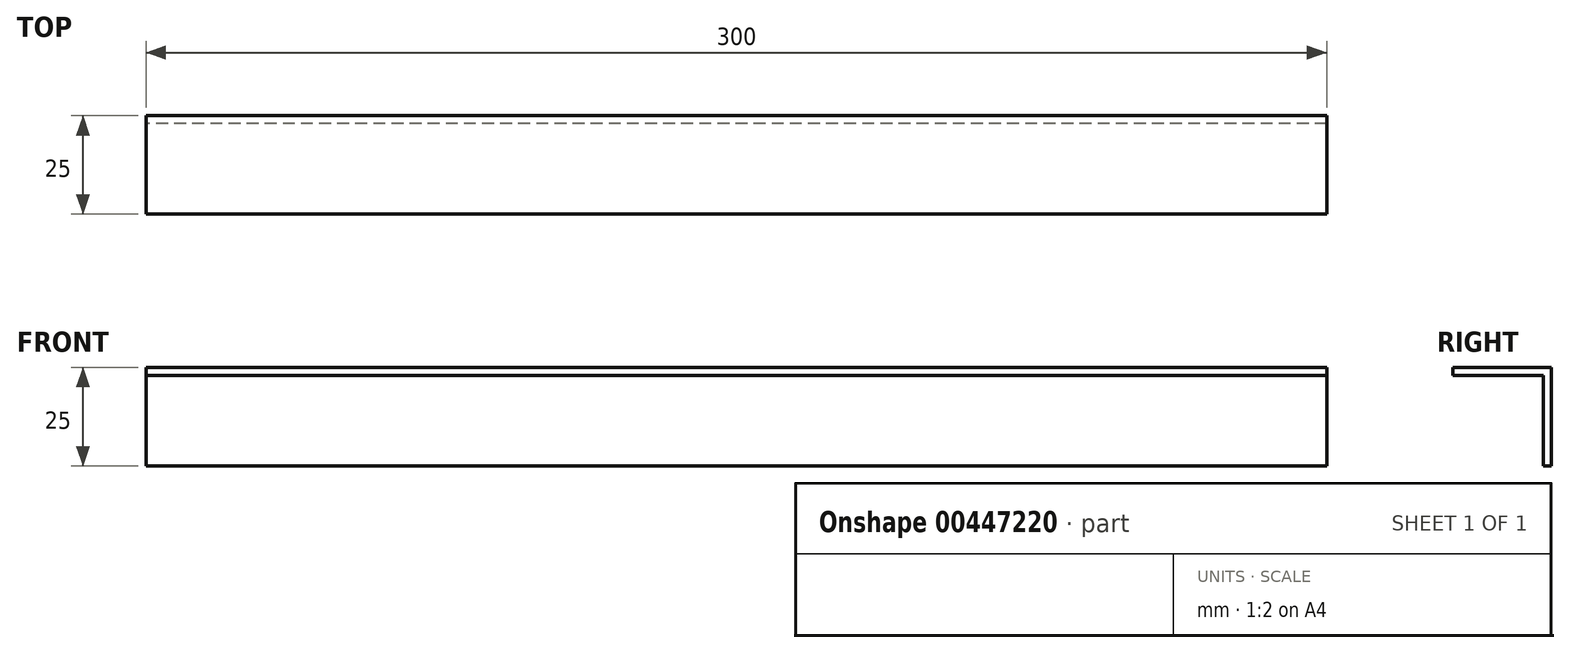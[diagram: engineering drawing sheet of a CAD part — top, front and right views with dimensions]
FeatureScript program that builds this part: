
annotation { "Feature Type Name" : "Feature", "Feature Type Description" : "" }
export const myFeature = defineFeature(function(context is Context, id is Id, definition is map)
    precondition{}
    {
        {
            var Q0;
            Q0=qCreatedBy(makeId("Top.planeOp"),FACE);
            var sketch = newSketch(context, id + "F0", { "sketchPlane" : qUnion([Q0])});
            skCircle(sketch, "E0", {"center": v(0, 0) * mm, "radius": 300 * mm, "construction": true});
            skPoint(sketch, "E1", {"position": v(150, -259.8) * mm});
            skSolve(sketch);
        }
        {
            var Q0;
            Q0=qCreatedBy(makeId("Right.planeOp"),FACE);
            var sketch = newSketch(context, id + "F1", { "sketchPlane" : qUnion([Q0])});
            skLineSegment(sketch, "E2", {"start": v(-259.8, 0) * mm, "end": v(-234.8, 0) * mm});
            skLineSegment(sketch, "E3", {"start": v(-234.8, 0) * mm, "end": v(-234.8, -25) * mm});
            skLineSegment(sketch, "E4", {"start": v(-234.8, -25) * mm, "end": v(-236.8, -25) * mm});
            skLineSegment(sketch, "E5", {"start": v(-236.8, -25) * mm, "end": v(-236.8, -2) * mm});
            skLineSegment(sketch, "E6", {"start": v(-236.8, -2) * mm, "end": v(-259.8, -2) * mm});
            skLineSegment(sketch, "E7", {"start": v(-259.8, -2) * mm, "end": v(-259.8, 0) * mm});
            skSolve(sketch);
        }
        {
            var Q0;
            Q0 = qSketchRegion(id + "F1", true);
            var Q1;
            Q1=sQuery(id+"F0.wireOp",VERTEX,"E1");
            extrude(context, id + "F2", {"entities" : qUnion([Q0]), "endBound" : BoundingType.UP_TO_VERTEX, "depth" : 25 * mm, "endBoundEntityVertex" : qUnion([Q1]), "offsetDistance" : 25 * mm});
        }
        {
            var Q0;
            Q0=makeQuery(id+"F2.opExtrude","SWEPT_BODY",BODY,{"disambiguationData":[OSD([sQuery(id+"F1.wireOp",EDGE,"E2"),sQuery(id+"F1.wireOp",EDGE,"E3"),sQuery(id+"F1.wireOp",EDGE,"E4"),sQuery(id+"F1.wireOp",EDGE,"E5"),sQuery(id+"F1.wireOp",EDGE,"E6"),sQuery(id+"F1.wireOp",EDGE,"E7")])]});
            var Q1;
            Q1=qCreatedBy(makeId("Right.planeOp"),FACE);
            mirror(context, id + "F3", {"operationType" : NewBodyOperationType.ADD, "entities" : qUnion([Q0]), "mirrorPlane" : qUnion([Q1])});
        }
    });
